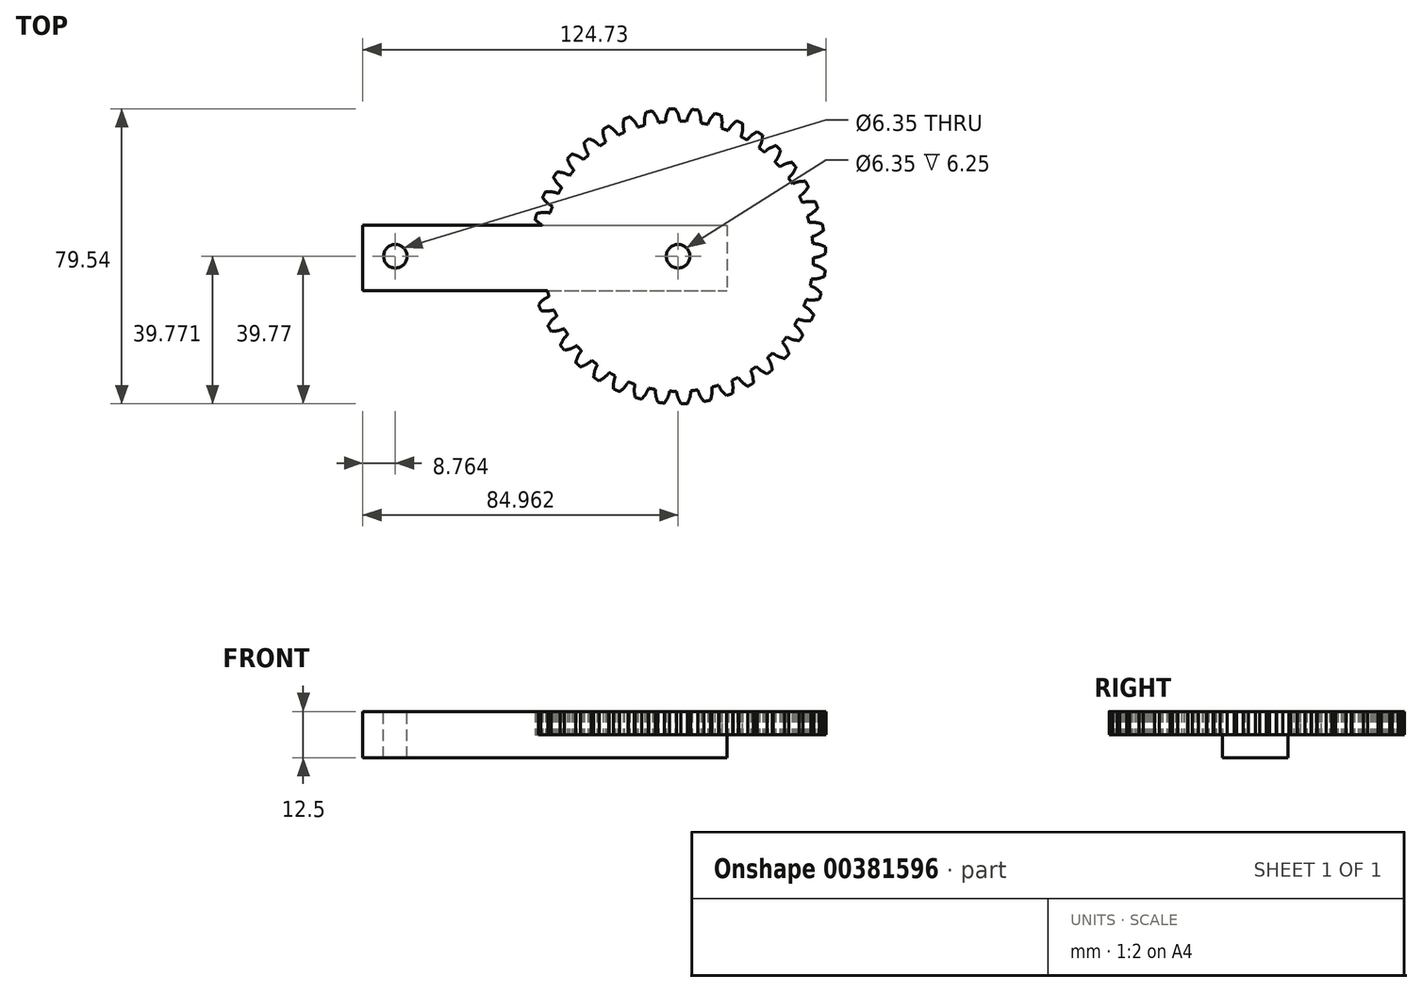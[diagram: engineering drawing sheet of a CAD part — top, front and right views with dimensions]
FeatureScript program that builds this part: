
annotation { "Feature Type Name" : "Feature", "Feature Type Description" : "" }
export const myFeature = defineFeature(function(context is Context, id is Id, definition is map)
    precondition{}
    {
        {
            var Q0;
            Q0=qCreatedBy(makeId("Top.planeOp"),FACE);
            var sketch = newSketch(context, id + "F0", { "sketchPlane" : qUnion([Q0])});
            skCircle(sketch, "E0", {"center": v(0, 0) * mm, "radius": 38.1 * mm, "construction": true});
            skLineSegment(sketch, "E1", {"start": v(0, 0) * mm, "end": v(0, 54.47) * mm, "construction": true});
            skLineSegment(sketch, "E2", {"start": v(-40.8, 38.1) * mm, "end": v(45.04, 38.1) * mm, "construction": true});
            skLineSegment(sketch, "E3", {"start": v(-12.24, 33.64) * mm, "end": v(18.8, 44.94) * mm, "construction": true});
            skLineSegment(sketch, "E4", {"start": v(0, 0) * mm, "end": v(-12.24, 33.64) * mm, "construction": true});
            skCircle(sketch, "E5", {"center": v(0, 0) * mm, "radius": 35.8 * mm, "construction": true});
            skPoint(sketch, "E6", {"position": v(-12.24, 33.64) * mm});
            skPoint(sketch, "E7", {"position": v(0, 38.1) * mm});
            skPoint(sketch, "E8", {"position": v(-16.8, 31.61) * mm});
            skLineSegment(sketch, "E9", {"start": v(-16.8, 31.61) * mm, "end": v(-0.9, 40.1) * mm, "construction": true});
            skArc(sketch, "E10", {"start": v(-7.44, 35.02) * mm, "mid": v(-9.87, 34.42) * mm, "end": v(-12.24, 33.64) * mm});
            skArc(sketch, "E11", {"start": v(-12.24, 33.64) * mm, "mid": v(-14.56, 32.7) * mm, "end": v(-16.8, 31.61) * mm});
            skLineSegment(sketch, "E12", {"start": v(-7.44, 35.02) * mm, "end": v(0.41, 36.69) * mm, "construction": true});
            skLineSegment(sketch, "E13", {"start": v(0, 38.1) * mm, "end": v(0, 0) * mm, "construction": true});
            skLineSegment(sketch, "E14", {"start": v(0.41, 36.69) * mm, "end": v(0.43, 36.44) * mm});
            skArc(sketch, "E15.trimOffspring", {"start": v(0, 36.44) * mm, "mid": v(0, 36.44) * mm, "end": v(0, 36.44) * mm});
            skLineSegment(sketch, "E16", {"start": v(0, 0) * mm, "end": v(-1.9, 46.38) * mm, "construction": true});
            skLineSegment(sketch, "E17.0.MirrorCS", {"start": v(5.36, 0.33) * mm, "end": v(1.52, 46.59) * mm, "construction": true});
            skLineSegment(sketch, "E18.0.MirrorCS", {"start": v(-3.43, 36.53) * mm, "end": v(-3.42, 36.28) * mm});
            skArc(sketch, "E19.converted", {"start": v(-3.42, 36.28) * mm, "mid": v(1.5, -36.41) * mm, "end": v(0.43, 36.44) * mm});
            skLineSegment(sketch, "E20", {"start": v(-3.42, 36.28) * mm, "end": v(-3.42, 36.28) * mm});
            skLineSegment(sketch, "E21", {"start": v(0.43, 36.44) * mm, "end": v(0.43, 36.44) * mm});
            skArc(sketch, "E22.trimOffspring", {"start": v(0.43, 36.44) * mm, "mid": v(-1.5, 36.41) * mm, "end": v(-3.42, 36.28) * mm});
            skArc(sketch, "E23.0", {"start": v(-0.74, 39.77) * mm, "mid": v(-1.64, 39.74) * mm, "end": v(-2.53, 39.7) * mm});
            skFitSpline(sketch, "E24.trimOffspring", {"points": [v(-2.4, 40.03) * mm, v(-3.13, 37.97) * mm, v(-3.43, 36.53) * mm], "startDerivative": vector(-1.5, -3.87) * mm, "endDerivative": vector(-0.5, -3.06) * mm});
            skFitSpline(sketch, "E25.trimOffspring", {"points": [v(-0.9, 40.1) * mm, v(0, 38.1) * mm, v(0.41, 36.69) * mm], "startDerivative": vector(1.82, -3.74) * mm, "endDerivative": vector(0.75, -3.01) * mm});
            skPoint(sketch, "E26.start.orphan", {"position": v(-0.86, 40.02) * mm});
            skPoint(sketch, "E27.trimOffspring.end.orphan", {"position": v(-2.43, 39.95) * mm});
            skCircle(sketch, "E28", {"center": v(0, 0) * mm, "radius": 3.17 * mm});
            skSolve(sketch);
        }
        {
            var Q0;
            Q0=qCreatedBy(makeId("Top.planeOp"),FACE);
            var sketch = newSketch(context, id + "F1", { "sketchPlane" : qUnion([Q0])});
            skFitSpline(sketch, "E29.0", {"points": [v(-2.4, 40.03) * mm, v(-2.68, 39.32) * mm, v(-3.18, 38.02) * mm, v(-3.35, 37) * mm, v(-3.43, 36.53) * mm]});
            skFitSpline(sketch, "E30.0", {"points": [v(-0.9, 40.1) * mm, v(-0.56, 39.4) * mm, v(0.05, 38.15) * mm, v(0.3, 37.14) * mm, v(0.41, 36.69) * mm]});
            skLineSegment(sketch, "E30.1", {"start": v(0.41, 36.69) * mm, "end": v(0.43, 36.44) * mm});
            skLineSegment(sketch, "E30.2", {"start": v(-3.43, 36.53) * mm, "end": v(-3.42, 36.28) * mm});
            skArc(sketch, "E30.3", {"start": v(-0.74, 39.77) * mm, "mid": v(-1.64, 39.74) * mm, "end": v(-2.53, 39.7) * mm});
            skArc(sketch, "E31.0", {"start": v(-3.42, 36.28) * mm, "mid": v(1.5, -36.41) * mm, "end": v(0.43, 36.44) * mm});
            skSolve(sketch);
        }
        {
            var Q0;
            Q0=makeQuery(id+"F1.imprint","IMPRINT",FACE,{"disambiguationData":[TD([[makeQuery(id+"F1.imprint","IMPRINT",EDGE,{"derivedFrom":sQuery(id+"F1.wireOp",EDGE,"E29.0")}),1.0]])]});
            extrude(context, id + "F2", {"entities" : qUnion([Q0]), "depth" : 25 / 4 * mm});
        }
        {
            var Q0;
            Q0=makeQuery(id+"F2.opExtrude","CAP_FACE",FACE,{"disambiguationData":[OSD([sQuery(id+"F1.wireOp",EDGE,"E29.0"),sQuery(id+"F1.wireOp",EDGE,"E30.0"),sQuery(id+"F1.wireOp",EDGE,"E30.1"),sQuery(id+"F1.wireOp",EDGE,"E30.2"),sQuery(id+"F1.wireOp",EDGE,"E30.3"),sQuery(id+"F1.wireOp",EDGE,"E31.0")])],"isStart":false});
            var Q1;
            Q1=makeQuery(id+"F2.opExtrude","SWEPT_BODY",BODY,{"disambiguationData":[OSD([sQuery(id+"F1.wireOp",EDGE,"E29.0"),sQuery(id+"F1.wireOp",EDGE,"E30.0"),sQuery(id+"F1.wireOp",EDGE,"E30.1"),sQuery(id+"F1.wireOp",EDGE,"E30.2"),sQuery(id+"F1.wireOp",EDGE,"E30.3"),sQuery(id+"F1.wireOp",EDGE,"E31.0")])]});
            var Q2;
            Q2=sQuery(id+"F1.wireOp",EDGE,"E31.0");
            circularPattern(context, id + "F3", {"entities" : qUnion([Q1]), "axis" : qUnion([Q2]), "angle" : 360 * degree, "instanceCount" : 40, "equalSpace" : true, "operationType" : NewBodyOperationType.ADD});
        }
        {
            var Q0;
            Q0=qCreatedBy(makeId("Top.planeOp"),FACE);
            var sketch = newSketch(context, id + "F4", { "sketchPlane" : qUnion([Q0])});
            skCircle(sketch, "E32", {"center": v(0, 0) * mm, "radius": 3.17 * mm});
            skLineSegment(sketch, "E33", {"start": v(-38.1, 43.64) * mm, "end": v(-38.1, -32.57) * mm, "construction": true});
            skCircle(sketch, "E34.0.MirrorC", {"center": v(-76.2, 0) * mm, "radius": 3.17 * mm});
            skLineSegment(sketch, "E35.bottom", {"start": v(-84.96, 8.41) * mm, "end": v(13.2, 8.41) * mm});
            skLineSegment(sketch, "E35.top", {"start": v(-84.96, -9.3) * mm, "end": v(13.2, -9.3) * mm});
            skLineSegment(sketch, "E35.left", {"start": v(-84.96, 8.41) * mm, "end": v(-84.96, -9.3) * mm});
            skLineSegment(sketch, "E35.right", {"start": v(13.2, 8.41) * mm, "end": v(13.2, -9.3) * mm});
            skLineSegment(sketch, "E36", {"start": v(-76.2, 0) * mm, "end": v(0, 0) * mm, "construction": true});
            skSolve(sketch);
        }
        {
            var Q0;
            Q0=makeQuery(id+"F4.imprint","IMPRINT",FACE,{"disambiguationData":[TD([[makeQuery(id+"F4.imprint","IMPRINT",EDGE,{"derivedFrom":sQuery(id+"F4.wireOp",EDGE,"E32")}),-1.0]])]});
            var Q1;
            Q1=makeQuery(id+"F4.imprint","IMPRINT",FACE,{"disambiguationData":[TD([[makeQuery(id+"F4.imprint","IMPRINT",EDGE,{"derivedFrom":sQuery(id+"F4.wireOp",EDGE,"E34.0.MirrorC")}),-1.0]])]});
            var Q2;
            Q2=makeQuery(id+"F4.imprint","IMPRINT",FACE,{"disambiguationData":[TD([[makeQuery(id+"F4.imprint","IMPRINT",EDGE,{"derivedFrom":sQuery(id+"F4.wireOp",EDGE,"E32")}),1.0]])]});
            extrude(context, id + "F5", {"entities" : qUnion([Q0, Q1, Q2]), "oppositeDirection" : true, "depth" : 25 / 4 * mm});
        }
        {
            var Q0;
            Q0=makeQuery(id+"F4.imprint","IMPRINT",FACE,{"disambiguationData":[TD([[makeQuery(id+"F4.imprint","IMPRINT",EDGE,{"derivedFrom":sQuery(id+"F4.wireOp",EDGE,"E34.0.MirrorC")}),-1.0]])]});
            var Q1;
            Q1=makeQuery(id+"F4.imprint","IMPRINT",FACE,{"disambiguationData":[TD([[makeQuery(id+"F4.imprint","IMPRINT",EDGE,{"derivedFrom":sQuery(id+"F4.wireOp",EDGE,"E32")}),1.0]])]});
            extrude(context, id + "F6", {"entities" : qUnion([Q0, Q1]), "operationType" : NewBodyOperationType.ADD, "depth" : 25 / 4 * mm});
        }
        {
            var Q0;
            Q0=makeQuery(id+"F0.imprint","IMPRINT",FACE,{"disambiguationData":[TD([[makeQuery(id+"F0.imprint","IMPRINT",EDGE,{"derivedFrom":sQuery(id+"F0.wireOp",EDGE,"E28")}),1.0]])]});
            extrude(context, id + "F7", {"entities" : qUnion([Q0]), "operationType" : NewBodyOperationType.REMOVE, "depth" : 25 * mm});
        }
    });
